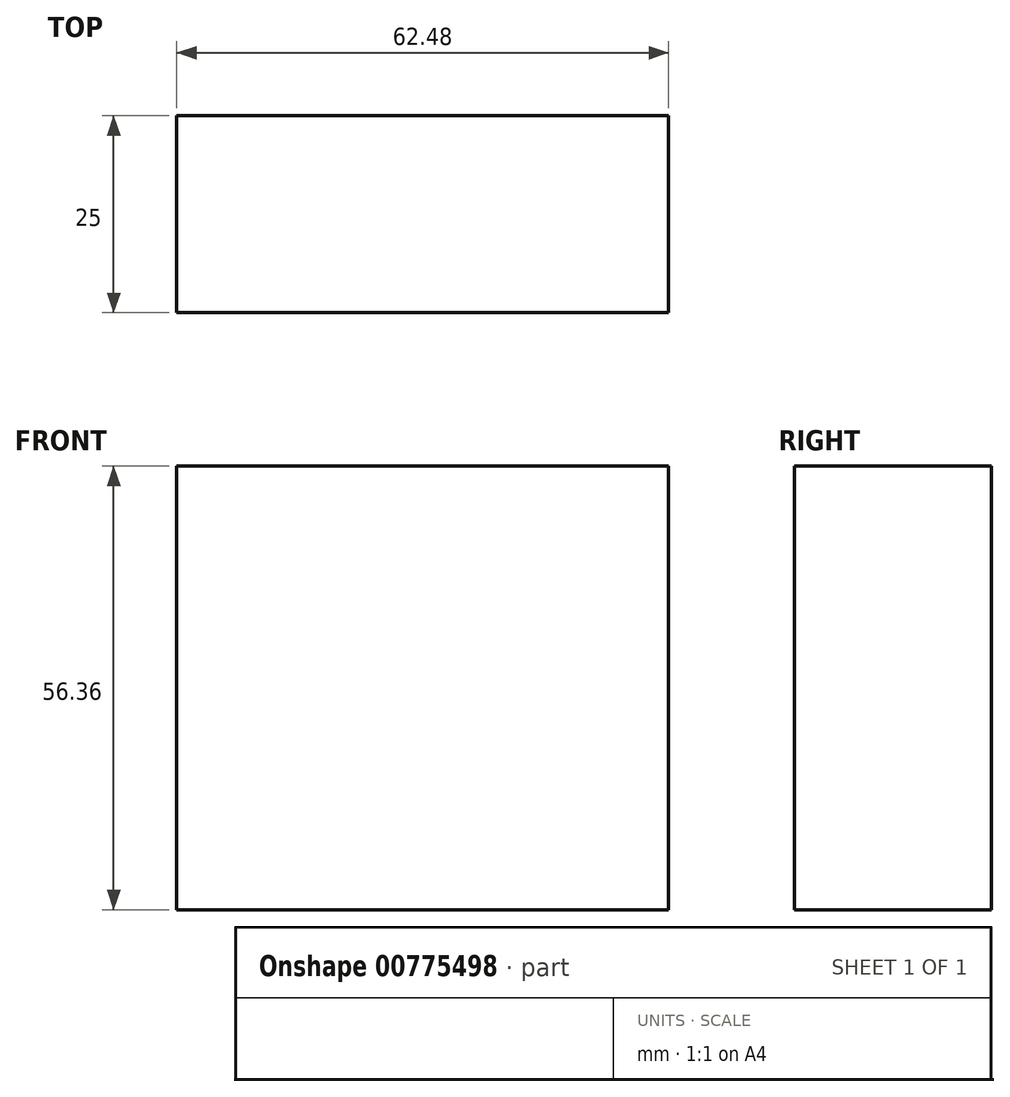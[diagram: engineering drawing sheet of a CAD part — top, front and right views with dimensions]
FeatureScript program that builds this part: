
annotation { "Feature Type Name" : "Feature", "Feature Type Description" : "" }
export const myFeature = defineFeature(function(context is Context, id is Id, definition is map)
    precondition{}
    {
        {
            var Q0;
            Q0=qCreatedBy(makeId("Front.planeOp"),FACE);
            var sketch = newSketch(context, id + "F0", { "sketchPlane" : qUnion([Q0])});
            skLineSegment(sketch, "E0.bottom", {"start": v(-31.24, 28.18) * mm, "end": v(31.24, 28.18) * mm});
            skLineSegment(sketch, "E0.top", {"start": v(-31.24, -28.18) * mm, "end": v(31.24, -28.18) * mm});
            skLineSegment(sketch, "E0.left", {"start": v(-31.24, 28.18) * mm, "end": v(-31.24, -28.18) * mm});
            skLineSegment(sketch, "E0.right", {"start": v(31.24, 28.18) * mm, "end": v(31.24, -28.18) * mm});
            skPoint(sketch, "E0.middle", {"position": v(0, 0) * mm});
            skSolve(sketch);
        }
        {
            var Q0;
            Q0=makeQuery(id+"F0.imprint","IMPRINT",FACE,{"disambiguationData":[TD([[makeQuery(id+"F0.imprint","IMPRINT",EDGE,{"derivedFrom":sQuery(id+"F0.wireOp",EDGE,"E0.bottom")}),-1.0]])]});
            extrude(context, id + "F1", {"entities" : qUnion([Q0]), "depth" : 25 * mm, "offsetDistance" : 25 * mm});
        }
    });
